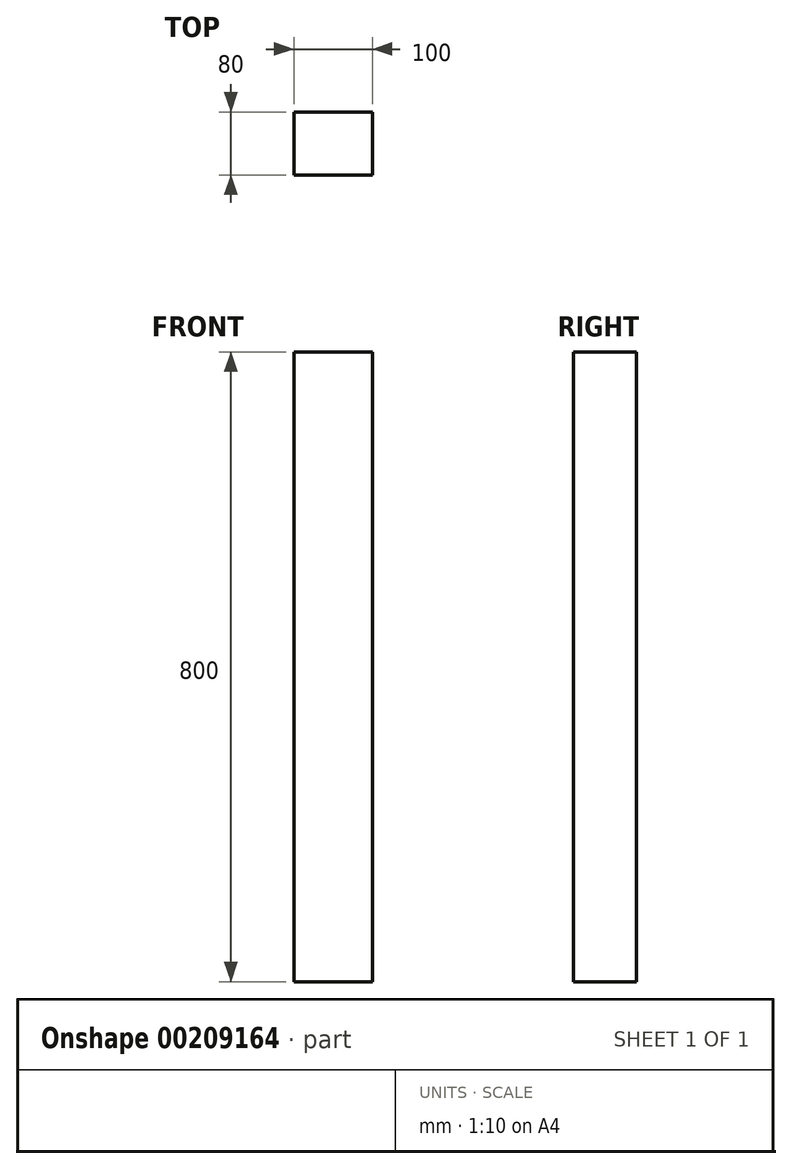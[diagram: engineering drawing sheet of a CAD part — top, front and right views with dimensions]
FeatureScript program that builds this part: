
annotation { "Feature Type Name" : "Feature", "Feature Type Description" : "" }
export const myFeature = defineFeature(function(context is Context, id is Id, definition is map)
    precondition{}
    {
        {
            var Q0;
            Q0=qCreatedBy(makeId("Front.planeOp"),FACE);
            var sketch = newSketch(context, id + "F0", { "sketchPlane" : qUnion([Q0])});
            skLineSegment(sketch, "E0.bottom", {"start": v(50, 400) * mm, "end": v(-50, 400) * mm});
            skLineSegment(sketch, "E0.top", {"start": v(50, -400) * mm, "end": v(-50, -400) * mm});
            skLineSegment(sketch, "E0.left", {"start": v(50, 400) * mm, "end": v(50, -400) * mm});
            skLineSegment(sketch, "E0.right", {"start": v(-50, 400) * mm, "end": v(-50, -400) * mm});
            skPoint(sketch, "E0.middle", {"position": v(0, 0) * mm});
            skSolve(sketch);
        }
        {
            var Q0;
            Q0 = qSketchRegion(id + "F0", true);
            extrude(context, id + "F1", {"entities" : qUnion([Q0]), "depth" : 80 * mm, "offsetDistance" : 25 * mm});
        }
    });
